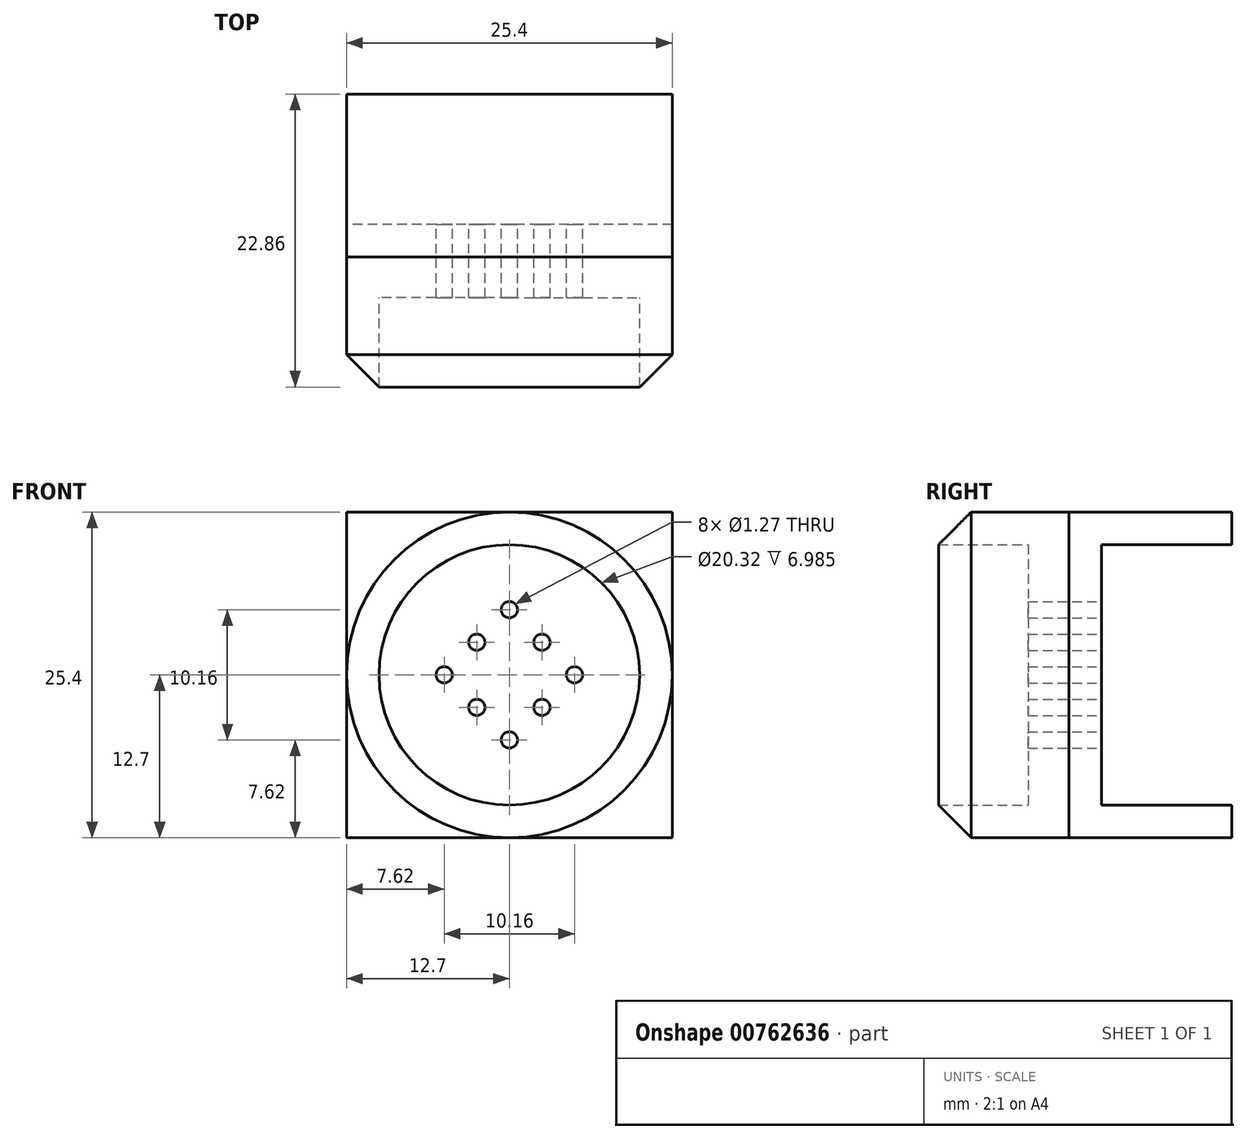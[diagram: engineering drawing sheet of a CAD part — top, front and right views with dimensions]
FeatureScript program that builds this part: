
annotation { "Feature Type Name" : "Feature", "Feature Type Description" : "" }
export const myFeature = defineFeature(function(context is Context, id is Id, definition is map)
    precondition{}
    {
        {
            var Q0;
            Q0=qCreatedBy(makeId("Front.planeOp"),FACE);
            var sketch = newSketch(context, id + "F0", { "sketchPlane" : qUnion([Q0])});
            skCircle(sketch, "E0", {"center": v(0, 0) * mm, "radius": 12.7 * mm});
            skCircle(sketch, "E1", {"center": v(0, 0) * mm, "radius": 10.16 * mm});
            skCircle(sketch, "E2", {"center": v(0, 5.08) * mm, "radius": 0.64 * mm});
            skCircle(sketch, "E3", {"center": v(2.54, 2.54) * mm, "radius": 0.64 * mm});
            skCircle(sketch, "E4", {"center": v(5.08, 0) * mm, "radius": 0.64 * mm});
            skCircle(sketch, "E5", {"center": v(-2.54, 2.54) * mm, "radius": 0.64 * mm});
            skCircle(sketch, "E6", {"center": v(-5.08, 0) * mm, "radius": 0.64 * mm});
            skCircle(sketch, "E7", {"center": v(-2.54, -2.54) * mm, "radius": 0.64 * mm});
            skCircle(sketch, "E8", {"center": v(0, -5.08) * mm, "radius": 0.64 * mm});
            skCircle(sketch, "E9", {"center": v(2.54, -2.54) * mm, "radius": 0.64 * mm});
            skSolve(sketch);
        }
        {
            var Q0;
            Q0=makeQuery(id+"F0.imprint","IMPRINT",FACE,{"disambiguationData":[TD([[makeQuery(id+"F0.imprint","IMPRINT",EDGE,{"derivedFrom":sQuery(id+"F0.wireOp",EDGE,"E0")}),1.0]])]});
            extrude(context, id + "F1", {"entities" : qUnion([Q0]), "depth" : 12.7 * mm, "offsetDistance" : 25.4 * mm});
        }
        {
            var Q0;
            Q0=makeQuery(id+"F0.imprint","IMPRINT",FACE,{"disambiguationData":[TD([[makeQuery(id+"F0.imprint","IMPRINT",EDGE,{"derivedFrom":sQuery(id+"F0.wireOp",EDGE,"E1")}),1.0]])]});
            extrude(context, id + "F2", {"entities" : qUnion([Q0]), "operationType" : NewBodyOperationType.ADD, "depth" : 3.17 * mm, "offsetDistance" : 25.4 * mm});
        }
        {
            var Q0;
            {var subQ0=sQuery(id+"F0.wireOp",EDGE,"E1");Q0=makeQuery(id+"F2.boolean.opBoolean","MERGE",FACE,{"derivedFrom":[makeQuery(id+"F1.opExtrude","CAP_FACE",FACE,{"disambiguationData":[OSD([sQuery(id+"F0.wireOp",EDGE,"E0"),subQ0])],"isStart":true}),makeQuery(id+"F2.opExtrude","CAP_FACE",FACE,{"disambiguationData":[OSD([subQ0,sQuery(id+"F0.wireOp",EDGE,"E2"),sQuery(id+"F0.wireOp",EDGE,"E3"),sQuery(id+"F0.wireOp",EDGE,"E4"),sQuery(id+"F0.wireOp",EDGE,"E5"),sQuery(id+"F0.wireOp",EDGE,"E6"),sQuery(id+"F0.wireOp",EDGE,"E7"),sQuery(id+"F0.wireOp",EDGE,"E8"),sQuery(id+"F0.wireOp",EDGE,"E9")])],"isStart":true})]});}
            var sketch = newSketch(context, id + "F3", { "sketchPlane" : qUnion([Q0])});
            skLineSegment(sketch, "E10.bottom", {"start": v(12.7, 12.7) * mm, "end": v(-12.7, 12.7) * mm});
            skLineSegment(sketch, "E10.top", {"start": v(12.7, -12.7) * mm, "end": v(-12.7, -12.7) * mm});
            skLineSegment(sketch, "E10.left", {"start": v(12.7, 12.7) * mm, "end": v(12.7, -12.7) * mm});
            skLineSegment(sketch, "E10.right", {"start": v(-12.7, 12.7) * mm, "end": v(-12.7, -12.7) * mm});
            skPoint(sketch, "E10.middle", {"position": v(0, 0) * mm});
            skLineSegment(sketch, "E11.top", {"start": v(-12.7, 10.16) * mm, "end": v(12.7, 10.16) * mm});
            skLineSegment(sketch, "E12.top", {"start": v(-12.7, -10.16) * mm, "end": v(12.7, -10.16) * mm});
            skSolve(sketch);
        }
        {
            var Q0;
            {var subQ0=sQuery(id+"F3.wireOp",EDGE,"E10.right");var subQ1=sQuery(id+"F3.wireOp",EDGE,"E10.bottom");var subQ2=makeQuery(id+"F3.imprint","INTERSECT",VERTEX,{"derivedFrom":[subQ1,subQ0]});Q0=makeQuery(id+"F3.imprint","IMPRINT",FACE,{"disambiguationData":[TD([[makeQuery(id+"F3.imprint","IMPRINT",EDGE,{"disambiguationData":[TD([[subQ2,1.0]])],"derivedFrom":subQ1}),1.0]])]});}
            var Q1;
            {var subQ0=sQuery(id+"F3.wireOp",EDGE,"E11.top");var subQ1=makeQuery(id+"F1.opExtrude","CAP_EDGE",EDGE,{"disambiguationData":[OSD([sQuery(id+"F0.wireOp",EDGE,"E0")])],"isStart":true});var subQ2=makeQuery(id+"F3.imprint","INTERSECT",VERTEX,{"disambiguationData":[OD(0.0)],"derivedFrom":[subQ1,subQ0]});Q1=makeQuery(id+"F3.imprint","IMPRINT",FACE,{"disambiguationData":[TD([[makeQuery(id+"F3.imprint","IMPRINT",EDGE,{"disambiguationData":[TD([[subQ2,-1.0]])],"derivedFrom":subQ0}),1.0]])]});}
            var Q2;
            {var subQ0=sQuery(id+"F3.wireOp",EDGE,"E10.left");var subQ1=sQuery(id+"F3.wireOp",EDGE,"E10.bottom");var subQ2=makeQuery(id+"F3.imprint","INTERSECT",VERTEX,{"derivedFrom":[subQ1,subQ0]});Q2=makeQuery(id+"F3.imprint","IMPRINT",FACE,{"disambiguationData":[TD([[makeQuery(id+"F3.imprint","IMPRINT",EDGE,{"disambiguationData":[TD([[subQ2,-1.0]])],"derivedFrom":subQ1}),1.0]])]});}
            var Q3;
            {var subQ0=sQuery(id+"F3.wireOp",EDGE,"E10.left");var subQ1=sQuery(id+"F3.wireOp",EDGE,"E10.top");var subQ2=makeQuery(id+"F3.imprint","INTERSECT",VERTEX,{"derivedFrom":[subQ1,subQ0]});Q3=makeQuery(id+"F3.imprint","IMPRINT",FACE,{"disambiguationData":[TD([[makeQuery(id+"F3.imprint","IMPRINT",EDGE,{"disambiguationData":[TD([[subQ2,-1.0]])],"derivedFrom":subQ1}),-1.0]])]});}
            var Q4;
            {var subQ0=sQuery(id+"F3.wireOp",EDGE,"E12.top");var subQ1=makeQuery(id+"F1.opExtrude","CAP_EDGE",EDGE,{"disambiguationData":[OSD([sQuery(id+"F0.wireOp",EDGE,"E0")])],"isStart":true});var subQ2=makeQuery(id+"F3.imprint","INTERSECT",VERTEX,{"disambiguationData":[OD(0.0)],"derivedFrom":[subQ1,subQ0]});Q4=makeQuery(id+"F3.imprint","IMPRINT",FACE,{"disambiguationData":[TD([[makeQuery(id+"F3.imprint","IMPRINT",EDGE,{"disambiguationData":[TD([[subQ2,-1.0]])],"derivedFrom":subQ0}),-1.0]])]});}
            var Q5;
            {var subQ0=sQuery(id+"F3.wireOp",EDGE,"E10.right");var subQ1=sQuery(id+"F3.wireOp",EDGE,"E10.top");var subQ2=makeQuery(id+"F3.imprint","INTERSECT",VERTEX,{"derivedFrom":[subQ1,subQ0]});Q5=makeQuery(id+"F3.imprint","IMPRINT",FACE,{"disambiguationData":[TD([[makeQuery(id+"F3.imprint","IMPRINT",EDGE,{"disambiguationData":[TD([[subQ2,1.0]])],"derivedFrom":subQ1}),-1.0]])]});}
            extrude(context, id + "F4", {"entities" : qUnion([Q0, Q1, Q2, Q3, Q4, Q5]), "operationType" : NewBodyOperationType.ADD, "depth" : 12.7 * mm, "offsetDistance" : 25.4 * mm});
        }
        {
            var Q0;
            {var subQ0=sQuery(id+"F3.wireOp",EDGE,"E11.top");var subQ1=sQuery(id+"F3.wireOp",EDGE,"E10.right");var subQ2=makeQuery(id+"F3.imprint","INTERSECT",VERTEX,{"derivedFrom":[subQ1,subQ0]});Q0=makeQuery(id+"F3.imprint","IMPRINT",FACE,{"disambiguationData":[TD([[makeQuery(id+"F3.imprint","IMPRINT",EDGE,{"disambiguationData":[TD([[subQ2,-1.0]])],"derivedFrom":subQ1}),1.0]])]});}
            var Q1;
            {var subQ0=sQuery(id+"F3.wireOp",EDGE,"E12.top");var subQ1=sQuery(id+"F3.wireOp",EDGE,"E10.right");var subQ2=makeQuery(id+"F3.imprint","INTERSECT",VERTEX,{"derivedFrom":[subQ1,subQ0]});Q1=makeQuery(id+"F3.imprint","IMPRINT",FACE,{"disambiguationData":[TD([[makeQuery(id+"F3.imprint","IMPRINT",EDGE,{"disambiguationData":[TD([[subQ2,1.0]])],"derivedFrom":subQ1}),1.0]])]});}
            var Q2;
            {var subQ0=sQuery(id+"F3.wireOp",EDGE,"E11.top");var subQ1=sQuery(id+"F3.wireOp",EDGE,"E10.left");var subQ2=makeQuery(id+"F3.imprint","INTERSECT",VERTEX,{"derivedFrom":[subQ1,subQ0]});Q2=makeQuery(id+"F3.imprint","IMPRINT",FACE,{"disambiguationData":[TD([[makeQuery(id+"F3.imprint","IMPRINT",EDGE,{"disambiguationData":[TD([[subQ2,-1.0]])],"derivedFrom":subQ1}),-1.0]])]});}
            var Q3;
            {var subQ0=sQuery(id+"F3.wireOp",EDGE,"E12.top");var subQ1=sQuery(id+"F3.wireOp",EDGE,"E10.left");var subQ2=makeQuery(id+"F3.imprint","INTERSECT",VERTEX,{"derivedFrom":[subQ1,subQ0]});Q3=makeQuery(id+"F3.imprint","IMPRINT",FACE,{"disambiguationData":[TD([[makeQuery(id+"F3.imprint","IMPRINT",EDGE,{"disambiguationData":[TD([[subQ2,1.0]])],"derivedFrom":subQ1}),-1.0]])]});}
            var Q4;
            Q4=makeQuery(id+"F3.imprint","IMPRINT",FACE,{"disambiguationData":[TD([[makeQuery(id+"F3.imprint","IMPRINT",EDGE,{"derivedFrom":makeQuery(id+"F2.opExtrude","CAP_EDGE",EDGE,{"disambiguationData":[OSD([sQuery(id+"F0.wireOp",EDGE,"E2")])],"isStart":true})}),1.0]])]});
            extrude(context, id + "F5", {"entities" : qUnion([Q0, Q1, Q2, Q3, Q4]), "operationType" : NewBodyOperationType.ADD, "depth" : 2.54 * mm, "offsetDistance" : 25.4 * mm});
        }
        {
            var Q0;
            Q0=makeQuery(id+"F1.opExtrude","CAP_EDGE",EDGE,{"disambiguationData":[OSD([sQuery(id+"F0.wireOp",EDGE,"E0")])],"isStart":false});
            chamfer(context, id + "F6", {"entities" : qUnion([Q0]), "width" : 5.08 * mm, "tangentPropagation" : true});
        }
    });
